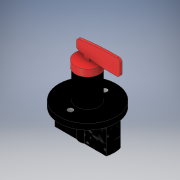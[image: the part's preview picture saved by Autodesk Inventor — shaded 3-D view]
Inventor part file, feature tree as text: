
AUTODESK INVENTOR PART (.ipt)
format: ipt  version: 2019 (Build 230136000, 136)  size: 189,440 bytes
history: native  units: in
note: dims shown in document units (in); Inventor stores cm internally (conversion verified against a paired STEP export)
features: extrude x8, sketch x8
ambient origin geometry x8: Origin, YZ Plane, XZ Plane, XY Plane, X Axis, Y Axis, Z Axis, Center Point
bodies: Solid1 (feature_tree)
feature tree (16):
  extrude  "Extrusion1"  Depth=0.25in TaperAngle=0.0deg
  extrude  "Extrusion3"  Depth=1.25in TaperAngle=0.0deg
  extrude  "Extrusion4"  Depth=0.25in
  extrude  "Extrusion5"  Depth=0.1in TaperAngle=0.0deg
  extrude  "Extrusion6"  Depth=0.125in
  extrude  "Extrusion7"  Depth=0.1in TaperAngle=0.0deg
  extrude  "Extrusion8"  Depth=1.156in TaperAngle=0.0deg
  extrude  "Extrusion9"  Depth=0.502in
  sketch  "Sketch1"  dims[d0=2.5in d1=0.25in d2=0.0in]
  sketch  "Sketch3"  dims[d9=1.0in d10=1.25in d11=0.0in]
  sketch  "Sketch4"  dims[d12=0.3in d13=0.0in d14=0.25in]
  sketch  "Sketch5"  dims[d15=0.1in d16=0.1in d17=0.0in]
  sketch  "Sketch6"  dims[d18=0.125in d19=0.125in]
  sketch  "Sketch7"  dims[d20=0.1in d21=0.0in d22=1.0in d23=0.0in]
  sketch  "Sketch8"  dims[d24=0.7in d25=1.156in d26=0.0in]
  sketch  "Sketch10"  dims[d31=0.502in d32=0.502in d33=0.23in d34=1.0in d35=0.0in]
